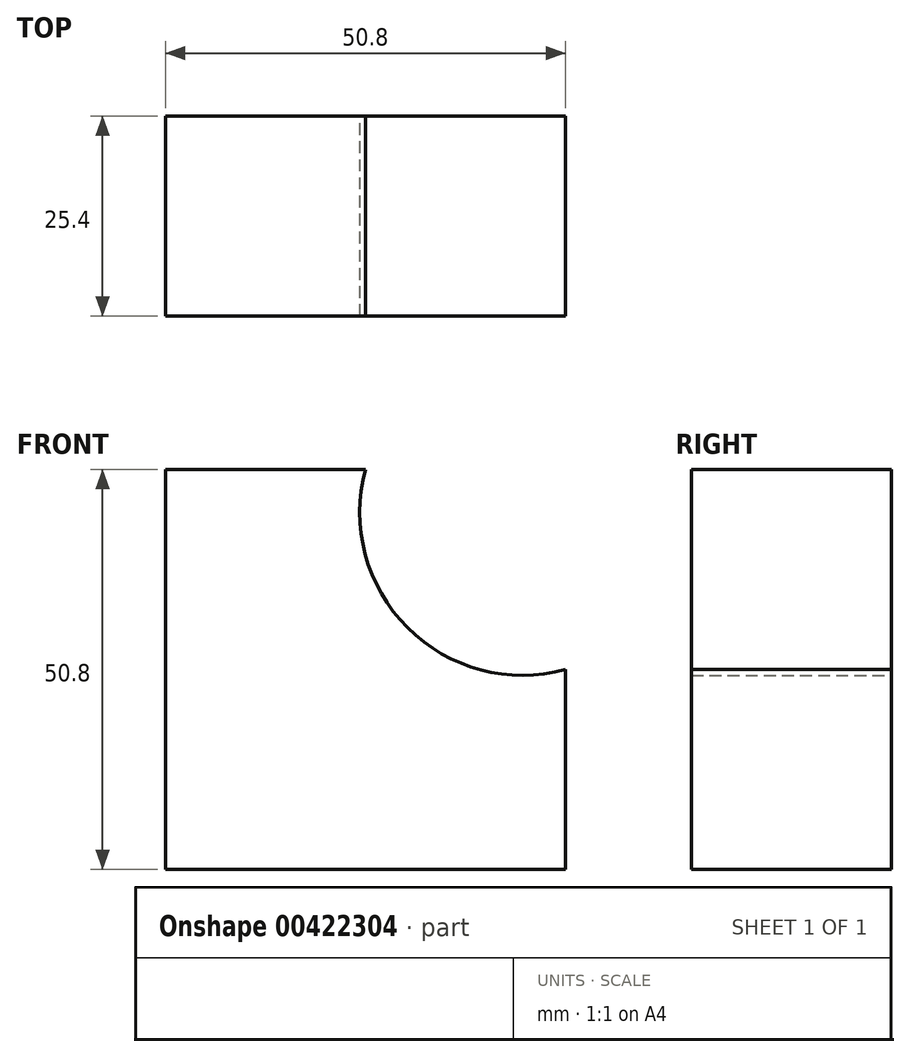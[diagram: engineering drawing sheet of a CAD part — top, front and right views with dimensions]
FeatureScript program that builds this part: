
annotation { "Feature Type Name" : "Feature", "Feature Type Description" : "" }
export const myFeature = defineFeature(function(context is Context, id is Id, definition is map)
    precondition{}
    {
        {
            var Q0;
            Q0=qCreatedBy(makeId("Front.planeOp"),FACE);
            var sketch = newSketch(context, id + "F0", { "sketchPlane" : qUnion([Q0])});
            skLineSegment(sketch, "E0", {"start": v(-59.52, 32.2) * mm, "end": v(-59.52, -18.6) * mm});
            skLineSegment(sketch, "E1", {"start": v(-59.52, -18.6) * mm, "end": v(-8.72, -18.6) * mm});
            skLineSegment(sketch, "E2", {"start": v(-8.72, -18.6) * mm, "end": v(-8.72, 6.8) * mm});
            skLineSegment(sketch, "E3", {"start": v(-59.52, 32.2) * mm, "end": v(-34.12, 32.2) * mm});
            skArc(sketch, "E4", {"start": v(-34.12, 32.2) * mm, "mid": v(-28.8, 12.12) * mm, "end": v(-8.72, 6.8) * mm});
            skSolve(sketch);
        }
        {
            var Q0;
            Q0 = qSketchRegion(id + "F0", true);
            extrude(context, id + "F1", {"entities" : qUnion([Q0]), "depth" : 25.4 * mm});
        }
    });
